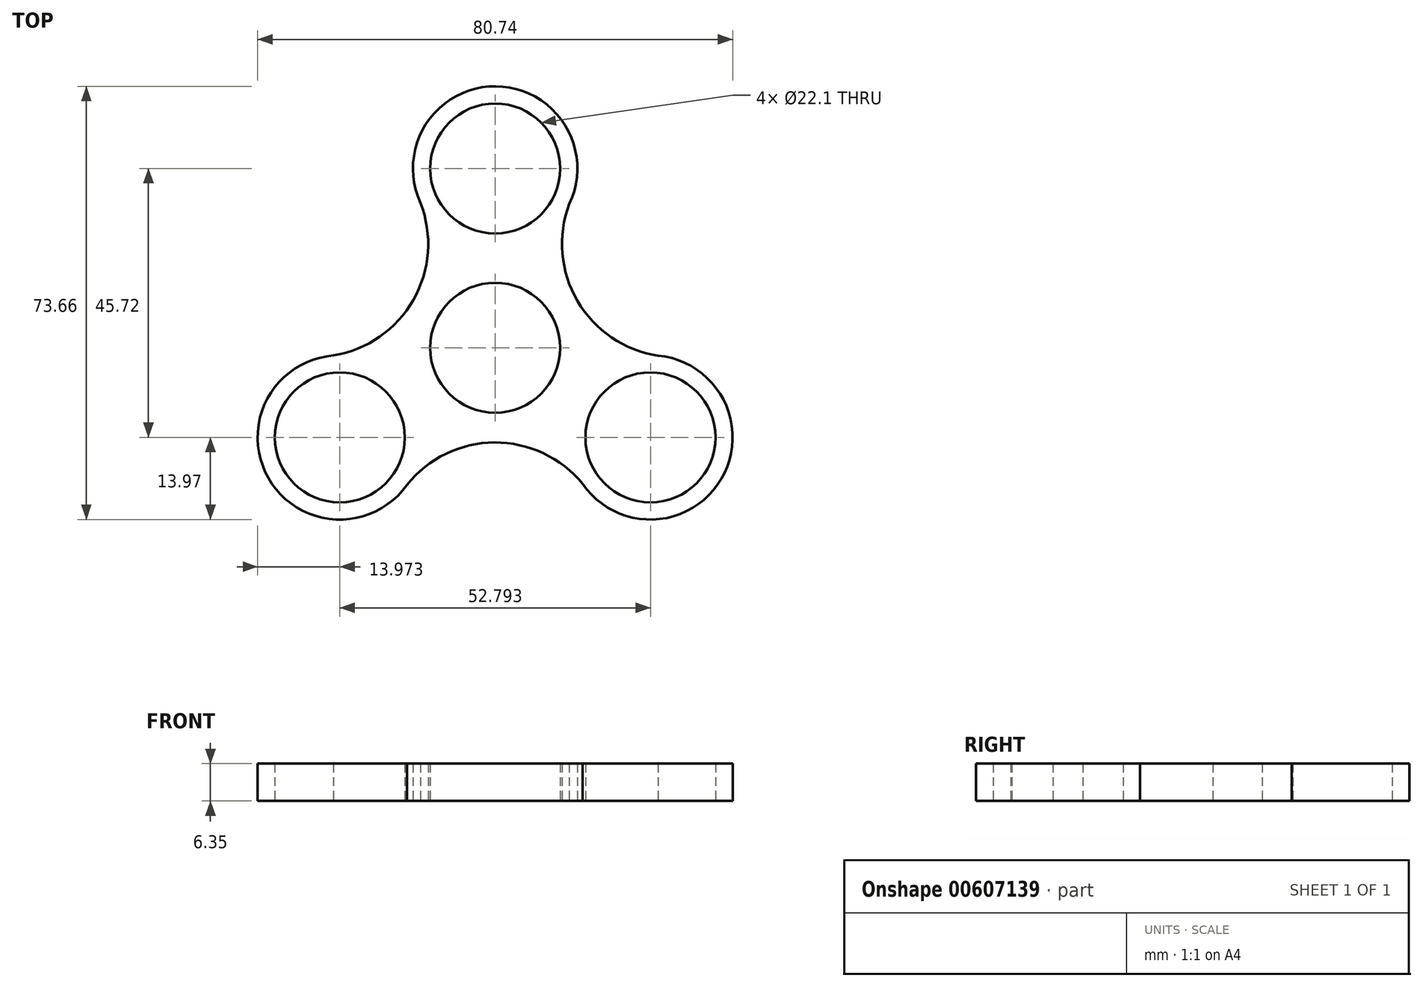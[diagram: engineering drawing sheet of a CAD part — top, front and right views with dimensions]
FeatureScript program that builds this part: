
annotation { "Feature Type Name" : "Feature", "Feature Type Description" : "" }
export const myFeature = defineFeature(function(context is Context, id is Id, definition is map)
    precondition{}
    {
        {
            var Q0;
            Q0=qCreatedBy(makeId("Top.planeOp"),FACE);
            var sketch = newSketch(context, id + "F0", { "sketchPlane" : qUnion([Q0])});
            skLineSegment(sketch, "E0", {"start": v(0, 0) * mm, "end": v(0, 30.48) * mm});
            skCircle(sketch, "E1", {"center": v(0, 30.48) * mm, "radius": 11.05 * mm});
            skCircle(sketch, "E2", {"center": v(0, 0) * mm, "radius": 11.05 * mm});
            skCircle(sketch, "E3.1.0", {"center": v(-26.4, -15.24) * mm, "radius": 11.05 * mm});
            skCircle(sketch, "E3.2.0", {"center": v(26.4, -15.24) * mm, "radius": 11.05 * mm});
            skArc(sketch, "E4", {"start": v(-27.46, -1.31) * mm, "mid": v(-38.55, -22.13) * mm, "end": v(-14.99, -23.3) * mm});
            skArc(sketch, "E5", {"start": v(14.87, -23.13) * mm, "mid": v(38.44, -22.32) * mm, "end": v(27.68, -1.33) * mm});
            skArc(sketch, "E6", {"start": v(12.6, 24.44) * mm, "mid": v(0.1, 44.45) * mm, "end": v(-12.69, 24.63) * mm});
            skArc(sketch, "E7", {"start": v(14.87, -23.13) * mm, "mid": v(-0.1, -16.1) * mm, "end": v(-14.99, -23.3) * mm});
            skArc(sketch, "E8.1.0", {"start": v(12.6, 24.44) * mm, "mid": v(14, 7.96) * mm, "end": v(27.68, -1.33) * mm});
            skArc(sketch, "E8.2.0", {"start": v(-27.46, -1.31) * mm, "mid": v(-13.9, 8.14) * mm, "end": v(-12.69, 24.63) * mm});
            skSolve(sketch);
        }
        {
            var Q0;
            Q0 = qSketchRegion(id + "F0", true);
            extrude(context, id + "F1", {"entities" : qUnion([Q0]), "depth" : 6.35 * mm, "offsetDistance" : 25.4 * mm});
        }
    });
